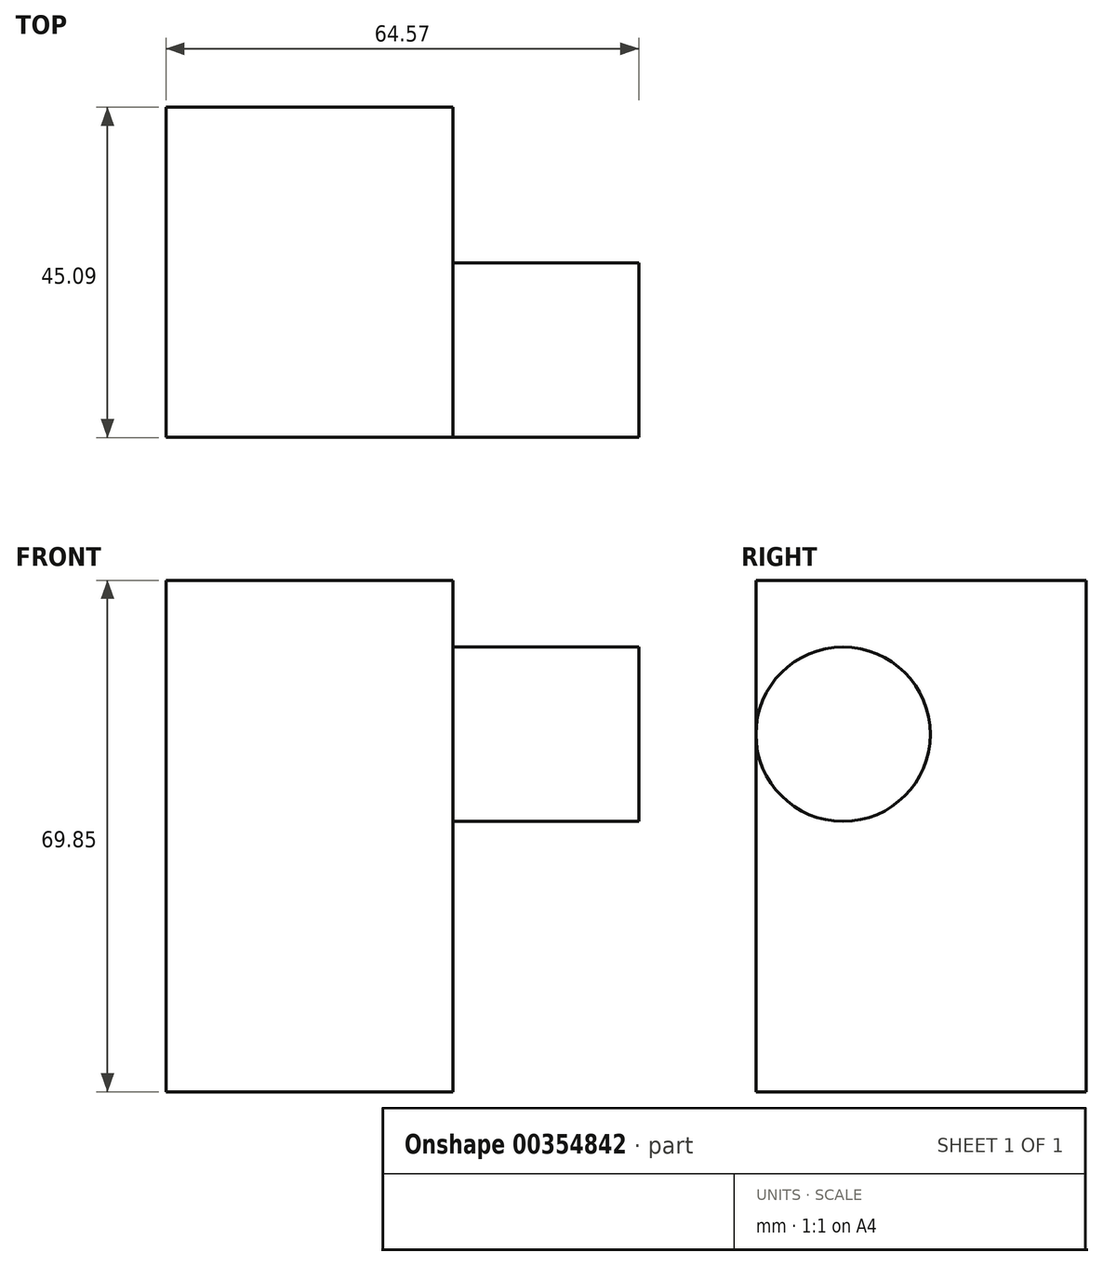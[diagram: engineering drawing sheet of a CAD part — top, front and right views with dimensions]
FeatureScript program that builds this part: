
annotation { "Feature Type Name" : "Feature", "Feature Type Description" : "" }
export const myFeature = defineFeature(function(context is Context, id is Id, definition is map)
    precondition{}
    {
        {
            var Q0;
            Q0=qCreatedBy(makeId("Top.planeOp"),FACE);
            var sketch = newSketch(context, id + "F0", { "sketchPlane" : qUnion([Q0])});
            skLineSegment(sketch, "E0.bottom", {"start": v(0, 0) * mm, "end": v(-39.17, 0) * mm});
            skLineSegment(sketch, "E0.top", {"start": v(0, -45.09) * mm, "end": v(-39.17, -45.09) * mm});
            skLineSegment(sketch, "E0.left", {"start": v(0, 0) * mm, "end": v(0, -45.09) * mm});
            skLineSegment(sketch, "E0.right", {"start": v(-39.17, 0) * mm, "end": v(-39.17, -45.09) * mm});
            skSolve(sketch);
        }
        {
            var Q0;
            Q0 = qSketchRegion(id + "F0", true);
            extrude(context, id + "F1", {"entities" : qUnion([Q0]), "depth" : 69.85 * mm});
        }
        {
            var Q0;
            Q0=makeQuery(id+"F1.opExtrude","SWEPT_FACE",FACE,{"disambiguationData":[OSD([sQuery(id+"F0.wireOp",EDGE,"E0.left")])]});
            var sketch = newSketch(context, id + "F2", { "sketchPlane" : qUnion([Q0])});
            skCircle(sketch, "E1", {"center": v(-33.18, 48.82) * mm, "radius": 11.9 * mm});
            skSolve(sketch);
        }
        {
            var Q0;
            Q0 = qSketchRegion(id + "F2", true);
            extrude(context, id + "F3", {"entities" : qUnion([Q0]), "operationType" : NewBodyOperationType.ADD, "depth" : 25.4 * mm});
        }
    });
